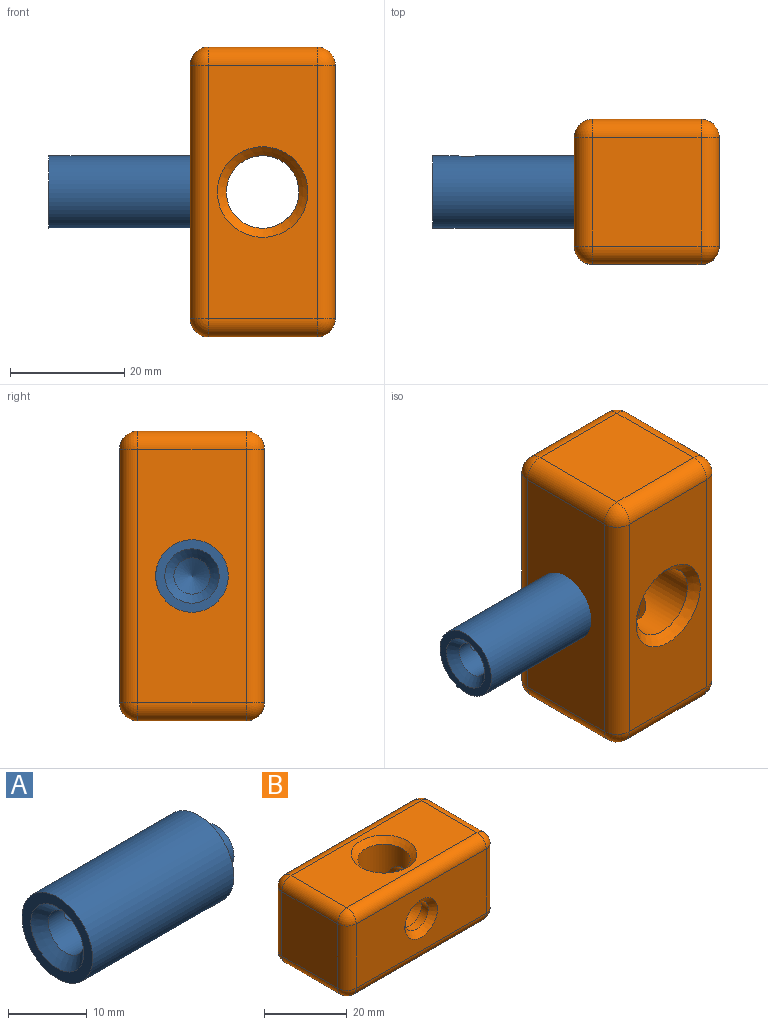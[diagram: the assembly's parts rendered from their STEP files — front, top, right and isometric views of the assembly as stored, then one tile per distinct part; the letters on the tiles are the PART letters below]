
ASSEMBLY  parts=2 mates=1
PART A: 9 faces, bbox 28.6x12.7x12.7 mm
  f0: cylinder r=6.35mm len=25.4mm, axis (-1,0,0), area 1005.4mm2, adj f2,f5,f7
  f1: cylinder r=3.17mm len=17.46mm, axis (-1,0,0), area 340.2mm2, adj f6,f7,f8
  f2: plane 12.7x12.7mm, normal (-1,0,0), area 55.4mm2, adj f0,f8
  f3: plane 6.35x6.35mm, normal (1,0,0), area 31.7mm2, adj f4
  f4: cylinder r=3.17mm len=6.35mm, axis (-1,0,0), area 63.3mm2, adj f3,f5
  f5: plane 12.7x12.7mm, normal (1,0,0), area 95mm2, adj f0,f4
  f6: cone r=0mm half-angle=59deg, axis (-1,0,0), area 36.9mm2, adj f1
  f7: cylinder r=1.59mm len=3.6mm, axis (0,-1,0), area 32.7mm2, adj f0,f1
  f8: cone r=3.17mm half-angle=45deg, axis (-1,0,0), area 56mm2, adj f1,f2
PART B: 35 faces, bbox 50.8x25.4x25.4 mm
  f0: cylinder r=6.35mm len=22.23mm, axis (0,0,-1), area 817.6mm2, adj f10,f11,f12
  f1: plane 19.05x19.05mm, normal (-1,0,0), area 362.9mm2, adj f23,f28,f31,f34
  f2: plane 44.45x19.05mm, normal (0,-1,0), area 749.8mm2, adj f13,f20,f29,f30,f34
  f3: plane 19.05x19.05mm, normal (1,0,0), area 265.9mm2, adj f14,f15,f19,f20,f21
  f4: plane 44.45x19.05mm, normal (0,1,0), area 846.8mm2, adj f15,f18,f22,f23
  f5: plane 44.45x19.05mm, normal (0,0,1), area 648.8mm2, adj f11,f18,f19,f28,f29
  f6: plane 44.45x19.05mm, normal (0,0,-1), area 648.8mm2, adj f12,f21,f22,f30,f31
  f7: cone r=0mm half-angle=59deg, axis (0,-1,0), area 57.7mm2, adj f8
  f8: cylinder r=3.97mm len=7.94mm, axis (0,-1,0), area 55.4mm2, adj f7,f13
  f9: cylinder r=3.97mm len=18.14mm, axis (1,0,0), area 452.4mm2, adj f10,f14
  f10: bspline ~11.11x8.88mm, area 52.1mm2, adj f0,f9
  f11: cone r=6.35mm half-angle=45deg, axis (0,0,1), area 100.8mm2, adj f0,f5
  f12: cone r=7.94mm half-angle=45deg, axis (0,0,-1), area 100.8mm2, adj f0,f6
  f13: cone r=3.97mm half-angle=45deg, axis (0,-1,0), area 67.2mm2, adj f2,f8
  f14: cone r=3.97mm half-angle=45deg, axis (1,0,0), area 67.2mm2, adj f3,f9
  f15: cylinder r=3.17mm len=19.05mm, axis (0,0,1), area 95mm2, adj f3,f4,f16,f17
  f16: sphere r=3.17mm, area 10.1mm2, adj f15,f18,f19
  f17: sphere r=3.17mm, area 10.1mm2, adj f15,f21,f22
  f18: cylinder r=3.17mm len=44.45mm, axis (1,0,0), area 221.7mm2, adj f4,f5,f16,f24
  f19: cylinder r=3.17mm len=19.05mm, axis (0,-1,0), area 95mm2, adj f3,f5,f16,f25
  f20: cylinder r=3.17mm len=19.05mm, axis (0,0,-1), area 95mm2, adj f2,f3,f25,f26
  f21: cylinder r=3.17mm len=19.05mm, axis (0,1,0), area 95mm2, adj f3,f6,f17,f26
  f22: cylinder r=3.17mm len=44.45mm, axis (-1,0,0), area 221.7mm2, adj f4,f6,f17,f27
  f23: cylinder r=3.17mm len=19.05mm, axis (0,0,-1), area 95mm2, adj f1,f4,f24,f27
  f24: sphere r=3.17mm, area 15.8mm2, adj f18,f23,f28
  f25: sphere r=3.17mm, area 15.8mm2, adj f19,f20,f29
  f26: sphere r=3.17mm, area 15.8mm2, adj f20,f21,f30
  f27: sphere r=3.17mm, area 21.6mm2, adj f22,f23,f31
  f28: cylinder r=3.17mm len=19.05mm, axis (0,1,0), area 95mm2, adj f1,f5,f24,f32
  f29: cylinder r=3.17mm len=44.45mm, axis (-1,0,0), area 221.7mm2, adj f2,f5,f25,f32
  f30: cylinder r=3.17mm len=44.45mm, axis (1,0,0), area 221.7mm2, adj f2,f6,f26,f33
  f31: cylinder r=3.17mm len=19.05mm, axis (0,-1,0), area 95mm2, adj f1,f6,f27,f33
  f32: sphere r=3.17mm, area 10.1mm2, adj f28,f29,f34
  f33: sphere r=3.17mm, area 15.8mm2, adj f30,f31,f34
  f34: cylinder r=3.17mm len=19.05mm, axis (0,0,1), area 95mm2, adj f1,f2,f32,f33
PLACE A t=(13.58,10.03,3.29)mm
PLACE B rot(axis=(0.58,0.58,-0.58),120deg) t=(39.19,22.73,3.29)mm
MATE fastened B.f7 <-> A.f0  axis (-1,0,0) through (30.3,10.03,3.29)mm
